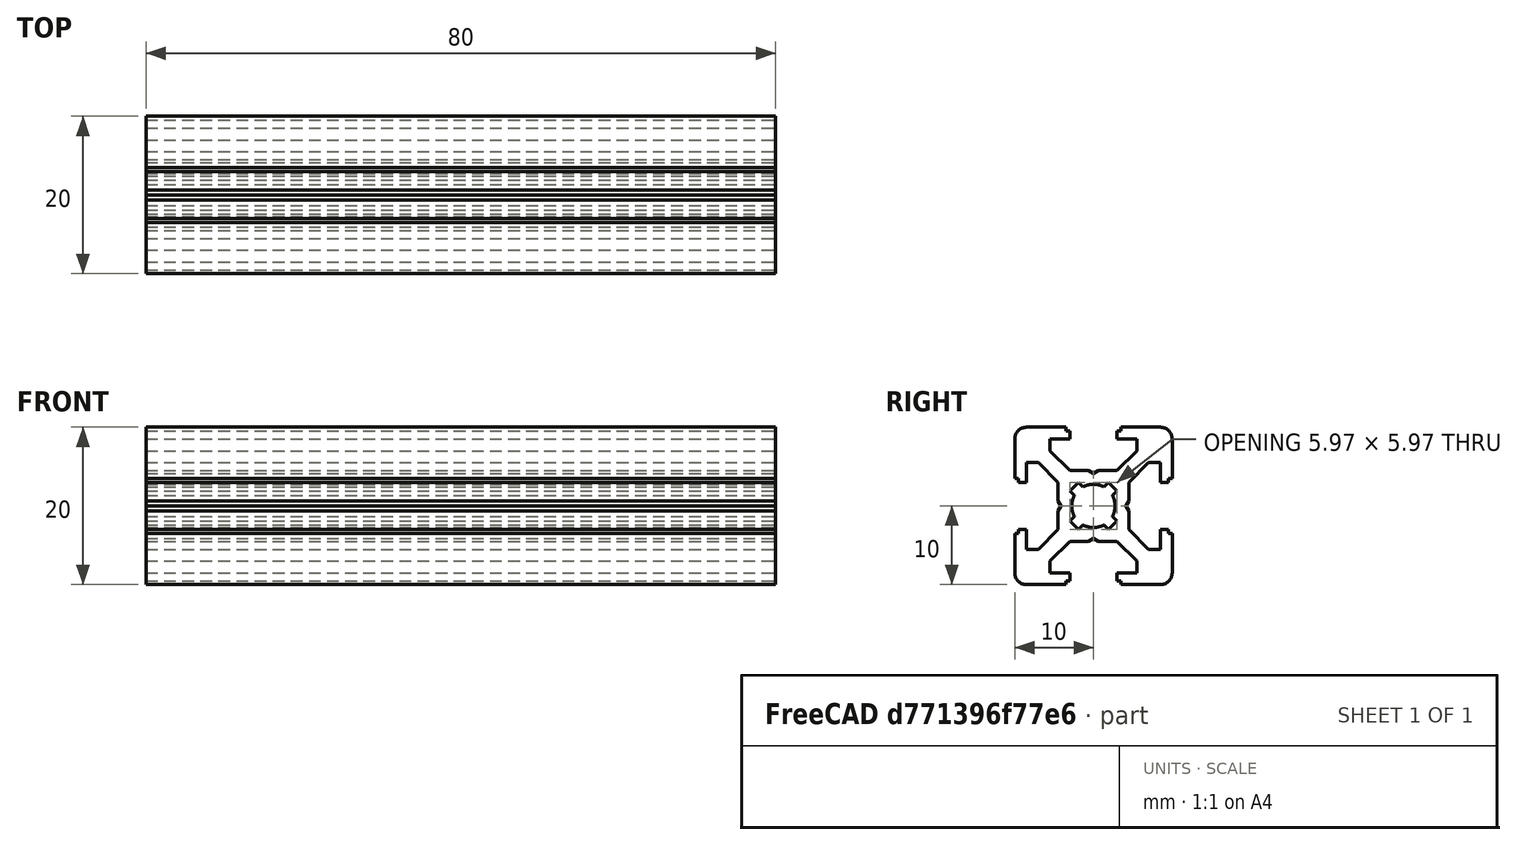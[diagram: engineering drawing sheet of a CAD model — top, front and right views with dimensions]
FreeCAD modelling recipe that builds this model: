
FCSTD DOCUMENT  (FreeCAD 0.19R)
Label: Tslot8
License: All rights reserved
LicenseURL: http://en.wikipedia.org/wiki/All_rights_reserved
objects: Sketcher::SketchObject×1, PartDesign::Pad×1, PartDesign::Body×1
note: 4 computed .brp shape members not serialized (recipe doc carries the construction recipe); baked Part::Feature solids carry a one-line shape summary decoded from their .brp

FEATURE [Sketcher::SketchObject] Sketch  label="T-Slot-Skizze"
  FullyConstrained = true
  MapMode = 5
  Placement = pos=(0,0,0) rot=(0.57735,0.57735,0.57735;2.0944rad)
  Support = -> [YZ_Plane]
  sketch-geometry (98):
    g0: LineSegment StartX=0 StartY=4.1 StartZ=0 EndX=0.65 EndY=4.5 EndZ=0
    g1: LineSegment StartX=0.65 StartY=4.5 StartZ=0 EndX=3 EndY=4.5 EndZ=0
    g2: LineSegment StartX=3 StartY=4.5 StartZ=0 EndX=5.5 EndY=7 EndZ=0
    g3: LineSegment StartX=5.5 StartY=7 StartZ=0 EndX=5.5 EndY=8.5 EndZ=0
    g4: LineSegment StartX=5.5 StartY=8.5 StartZ=0 EndX=3 EndY=8.5 EndZ=0
    g5: LineSegment StartX=3 StartY=8.5 StartZ=0 EndX=3 EndY=9.5 EndZ=0
    g6: LineSegment StartX=3 StartY=9.5 StartZ=0 EndX=3.5 EndY=9.5 EndZ=0
    g7: LineSegment StartX=3.5 StartY=9.5 StartZ=0 EndX=3.5 EndY=10 EndZ=0
    g8: LineSegment StartX=3.5 StartY=10 StartZ=0 EndX=8.5 EndY=10 EndZ=0
    g9: LineSegment StartX=10 StartY=8.5 StartZ=0 EndX=10 EndY=3.5 EndZ=0
    g10: LineSegment StartX=10 StartY=3.5 StartZ=0 EndX=9.5 EndY=3.5 EndZ=0
    g11: LineSegment StartX=9.5 StartY=3.5 StartZ=0 EndX=9.5 EndY=3 EndZ=0
    g12: LineSegment StartX=9.5 StartY=3 StartZ=0 EndX=8.5 EndY=3 EndZ=0
    g13: LineSegment StartX=8.5 StartY=3 StartZ=0 EndX=8.5 EndY=5.5 EndZ=0
    g14: LineSegment StartX=8.5 StartY=5.5 StartZ=0 EndX=7 EndY=5.5 EndZ=0
    g15: LineSegment StartX=7 StartY=5.5 StartZ=0 EndX=4.5 EndY=3 EndZ=0
    g16: LineSegment StartX=4.5 StartY=3 StartZ=0 EndX=4.5 EndY=0.65 EndZ=0
    g17: LineSegment StartX=4.5 StartY=0.65 StartZ=0 EndX=4.1 EndY=0 EndZ=0
    g18: ArcOfCircle CenterX=8.5 CenterY=8.5 CenterZ=0 NormalX=0 NormalY=0 NormalZ=1 AngleXU=0 Radius=1.5 StartAngle=0 EndAngle=1.5708
    g19: LineSegment StartX=0 StartY=-4.1 StartZ=0 EndX=0.65 EndY=-4.5 EndZ=0
    g20: LineSegment StartX=0.65 StartY=-4.5 StartZ=0 EndX=3 EndY=-4.5 EndZ=0
    g21: LineSegment StartX=3 StartY=-4.5 StartZ=0 EndX=5.5 EndY=-7 EndZ=0
    g22: LineSegment StartX=5.5 StartY=-7 StartZ=0 EndX=5.5 EndY=-8.5 EndZ=0
    g23: LineSegment StartX=5.5 StartY=-8.5 StartZ=0 EndX=3 EndY=-8.5 EndZ=0
    g24: LineSegment StartX=3 StartY=-8.5 StartZ=0 EndX=3 EndY=-9.5 EndZ=0
    g25: LineSegment StartX=3 StartY=-9.5 StartZ=0 EndX=3.5 EndY=-9.5 EndZ=0
    g26: LineSegment StartX=3.5 StartY=-9.5 StartZ=0 EndX=3.5 EndY=-10 EndZ=0
    g27: LineSegment StartX=3.5 StartY=-10 StartZ=0 EndX=8.5 EndY=-10 EndZ=0
    g28: LineSegment StartX=10 StartY=-8.5 StartZ=0 EndX=10 EndY=-3.5 EndZ=0
    g29: LineSegment StartX=10 StartY=-3.5 StartZ=0 EndX=9.5 EndY=-3.5 EndZ=0
    g30: LineSegment StartX=9.5 StartY=-3.5 StartZ=0 EndX=9.5 EndY=-3 EndZ=0
    g31: LineSegment StartX=9.5 StartY=-3 StartZ=0 EndX=8.5 EndY=-3 EndZ=0
    g32: LineSegment StartX=8.5 StartY=-3 StartZ=0 EndX=8.5 EndY=-5.5 EndZ=0
    g33: LineSegment StartX=8.5 StartY=-5.5 StartZ=0 EndX=7 EndY=-5.5 EndZ=0
    g34: LineSegment StartX=7 StartY=-5.5 StartZ=0 EndX=4.5 EndY=-3 EndZ=0
    g35: LineSegment StartX=4.5 StartY=-3 StartZ=0 EndX=4.5 EndY=-0.65 EndZ=0
    g36: ArcOfCircle CenterX=8.5 CenterY=-8.5 CenterZ=0 NormalX=0 NormalY=0 NormalZ=1 AngleXU=0 Radius=1.5 StartAngle=4.71239 EndAngle=6.28319
    g37: LineSegment StartX=4.5 StartY=-0.65 StartZ=0 EndX=4.1 EndY=0 EndZ=0
    g38: LineSegment StartX=0 StartY=-4.1 StartZ=0 EndX=-0.65 EndY=-4.5 EndZ=0
    g39: LineSegment StartX=-0.65 StartY=-4.5 StartZ=0 EndX=-3 EndY=-4.5 EndZ=0
    g40: LineSegment StartX=-3 StartY=-4.5 StartZ=0 EndX=-5.5 EndY=-7 EndZ=0
    g41: LineSegment StartX=-5.5 StartY=-7 StartZ=0 EndX=-5.5 EndY=-8.5 EndZ=0
    g42: LineSegment StartX=-5.5 StartY=-8.5 StartZ=0 EndX=-3 EndY=-8.5 EndZ=0
    g43: LineSegment StartX=-3 StartY=-8.5 StartZ=0 EndX=-3 EndY=-9.5 EndZ=0
    g44: LineSegment StartX=-3 StartY=-9.5 StartZ=0 EndX=-3.5 EndY=-9.5 EndZ=0
    g45: LineSegment StartX=-3.5 StartY=-9.5 StartZ=0 EndX=-3.5 EndY=-10 EndZ=0
    g46: LineSegment StartX=-3.5 StartY=-10 StartZ=0 EndX=-8.5 EndY=-10 EndZ=0
    g47: LineSegment StartX=-10 StartY=-8.5 StartZ=0 EndX=-10 EndY=-3.5 EndZ=0
    g48: LineSegment StartX=-10 StartY=-3.5 StartZ=0 EndX=-9.5 EndY=-3.5 EndZ=0
    g49: LineSegment StartX=-9.5 StartY=-3.5 StartZ=0 EndX=-9.5 EndY=-3 EndZ=0
    g50: LineSegment StartX=-9.5 StartY=-3 StartZ=0 EndX=-8.5 EndY=-3 EndZ=0
    g51: LineSegment StartX=-8.5 StartY=-3 StartZ=0 EndX=-8.5 EndY=-5.5 EndZ=0
    g52: LineSegment StartX=-8.5 StartY=-5.5 StartZ=0 EndX=-7 EndY=-5.5 EndZ=0
    g53: LineSegment StartX=-7 StartY=-5.5 StartZ=0 EndX=-4.5 EndY=-3 EndZ=0
    g54: LineSegment StartX=-4.5 StartY=-3 StartZ=0 EndX=-4.5 EndY=-0.65 EndZ=0
    g55: ArcOfCircle CenterX=-8.5 CenterY=-8.5 CenterZ=0 NormalX=0 NormalY=0 NormalZ=1 AngleXU=0 Radius=1.5 StartAngle=3.14159 EndAngle=4.71239
    g56: LineSegment StartX=-4.5 StartY=-0.65 StartZ=0 EndX=-4.1 EndY=0 EndZ=0
    g57: LineSegment StartX=-0.65 StartY=4.5 StartZ=0 EndX=-3 EndY=4.5 EndZ=0
    g58: LineSegment StartX=-3 StartY=4.5 StartZ=0 EndX=-5.5 EndY=7 EndZ=0
    g59: LineSegment StartX=-5.5 StartY=7 StartZ=0 EndX=-5.5 EndY=8.5 EndZ=0
    g60: LineSegment StartX=-5.5 StartY=8.5 StartZ=0 EndX=-3 EndY=8.5 EndZ=0
    g61: LineSegment StartX=-3 StartY=8.5 StartZ=0 EndX=-3 EndY=9.5 EndZ=0
    g62: LineSegment StartX=-3 StartY=9.5 StartZ=0 EndX=-3.5 EndY=9.5 EndZ=0
    g63: LineSegment StartX=-3.5 StartY=9.5 StartZ=0 EndX=-3.5 EndY=10 EndZ=0
    g64: LineSegment StartX=-3.5 StartY=10 StartZ=0 EndX=-8.5 EndY=10 EndZ=0
    g65: LineSegment StartX=-10 StartY=8.5 StartZ=0 EndX=-10 EndY=3.5 EndZ=0
    g66: LineSegment StartX=-10 StartY=3.5 StartZ=0 EndX=-9.5 EndY=3.5 EndZ=0
    g67: LineSegment StartX=-9.5 StartY=3.5 StartZ=0 EndX=-9.5 EndY=3 EndZ=0
    g68: LineSegment StartX=-9.5 StartY=3 StartZ=0 EndX=-8.5 EndY=3 EndZ=0
    g69: LineSegment StartX=-8.5 StartY=3 StartZ=0 EndX=-8.5 EndY=5.5 EndZ=0
    g70: LineSegment StartX=-8.5 StartY=5.5 StartZ=0 EndX=-7 EndY=5.5 EndZ=0
    g71: LineSegment StartX=-7 StartY=5.5 StartZ=0 EndX=-4.5 EndY=3 EndZ=0
    g72: LineSegment StartX=-4.5 StartY=3 StartZ=0 EndX=-4.5 EndY=0.65 EndZ=0
    g73: ArcOfCircle CenterX=-8.5 CenterY=8.5 CenterZ=0 NormalX=0 NormalY=0 NormalZ=1 AngleXU=0 Radius=1.5 StartAngle=1.5708 EndAngle=3.14159
    g74: LineSegment StartX=-4.5 StartY=0.65 StartZ=0 EndX=-4.1 EndY=0 EndZ=0
    g75: LineSegment StartX=0 StartY=4.1 StartZ=0 EndX=-0.65 EndY=4.5 EndZ=0
    g76: Circle CenterX=0 CenterY=0 CenterZ=0 NormalX=0 NormalY=0 NormalZ=1 AngleXU=0 Radius=3.55
    g77: Circle CenterX=0 CenterY=0 CenterZ=0 NormalX=0 NormalY=0 NormalZ=1 AngleXU=0 Radius=2.75
    g78: LineSegment StartX=1.3405 StartY=2.40116 StartZ=0 EndX=1.92324 EndY=2.9839 EndZ=0
    g79: LineSegment StartX=1.92324 StartY=2.9839 StartZ=0 EndX=2.9839 EndY=1.92324 EndZ=0
    g80: LineSegment StartX=2.9839 StartY=1.92324 StartZ=0 EndX=2.40116 EndY=1.3405 EndZ=0
    g81: ArcOfCircle CenterX=0 CenterY=0 CenterZ=0 NormalX=0 NormalY=0 NormalZ=1 AngleXU=0 Radius=2.75 StartAngle=0 EndAngle=0.509172
    g82: ArcOfCircle CenterX=0 CenterY=0 CenterZ=0 NormalX=0 NormalY=0 NormalZ=1 AngleXU=0 Radius=2.75 StartAngle=1.06162 EndAngle=1.5708
    g83: LineSegment StartX=-1.3405 StartY=2.40116 StartZ=0 EndX=-1.92324 EndY=2.9839 EndZ=0
    g84: LineSegment StartX=-1.92324 StartY=2.9839 StartZ=0 EndX=-2.9839 EndY=1.92324 EndZ=0
    g85: LineSegment StartX=-2.9839 StartY=1.92324 StartZ=0 EndX=-2.40116 EndY=1.3405 EndZ=0
    g86: ArcOfCircle CenterX=-1.3e-15 CenterY=6e-16 CenterZ=0 NormalX=0 NormalY=0 NormalZ=1 AngleXU=0 Radius=2.75 StartAngle=2.63242 EndAngle=3.14159
    g87: ArcOfCircle CenterX=-1.3e-15 CenterY=6e-16 CenterZ=0 NormalX=0 NormalY=0 NormalZ=1 AngleXU=0 Radius=2.75 StartAngle=1.5708 EndAngle=2.07997
    g88: LineSegment StartX=-1.34051 StartY=-2.40115 StartZ=0 EndX=-1.92325 EndY=-2.98389 EndZ=0
    g89: LineSegment StartX=-1.92325 StartY=-2.98389 StartZ=0 EndX=-2.9839 EndY=-1.92323 EndZ=0
    g90: LineSegment StartX=-2.9839 StartY=-1.92323 StartZ=0 EndX=-2.40116 EndY=-1.34049 EndZ=0
    g91: ArcOfCircle CenterX=-3e-16 CenterY=2e-16 CenterZ=0 NormalX=0 NormalY=0 NormalZ=1 AngleXU=0 Radius=2.75 StartAngle=3.14159 EndAngle=3.65076
    g92: ArcOfCircle CenterX=-3e-16 CenterY=2e-16 CenterZ=0 NormalX=0 NormalY=0 NormalZ=1 AngleXU=0 Radius=2.75 StartAngle=4.20321 EndAngle=4.71239
    g93: LineSegment StartX=1.34051 StartY=-2.40115 StartZ=0 EndX=1.92325 EndY=-2.98389 EndZ=0
    g94: LineSegment StartX=1.92325 StartY=-2.98389 StartZ=0 EndX=2.9839 EndY=-1.92323 EndZ=0
    g95: LineSegment StartX=2.9839 StartY=-1.92323 StartZ=0 EndX=2.40116 EndY=-1.34049 EndZ=0
    g96: ArcOfCircle CenterX=3e-16 CenterY=2e-16 CenterZ=0 NormalX=0 NormalY=0 NormalZ=1 AngleXU=0 Radius=2.75 StartAngle=4.71239 EndAngle=5.22156
    g97: ArcOfCircle CenterX=3e-16 CenterY=2e-16 CenterZ=0 NormalX=0 NormalY=0 NormalZ=1 AngleXU=0 Radius=2.75 StartAngle=5.77402 EndAngle=6.28319
  constraints (291):
    c: PointOnObject(g0,g-2)
    c: Coincident(g0,g1)
    c: Horizontal(g1)
    c: Coincident(g1,g2)
    c: Coincident(g2,g3)
    c: Vertical(g3)
    c: Coincident(g3,g4)
    c: Horizontal(g4)
    c: Coincident(g4,g5)
    c: Vertical(g5)
    c: Coincident(g5,g6)
    c: Horizontal(g6)
    c: Coincident(g6,g7)
    c: Coincident(g7,g8)
    c: Horizontal(g8)
    c: Vertical(g7)
    c: DistanceX(g-1,g5) = 3
    c: DistanceY(g4,g7) = 1.5
    c: DistanceY(g0,g7) = 5.5
    c: DistanceY(g3,g3) = 1.5
    c: DistanceY(g4,g5) = 1
    c: DistanceX(g-1,g1) = 3
    c: DistanceX(g-1,g7) = 3.5
    c: DistanceX(g0,g0) = 0.65
    c: DistanceY(g0,g0) = 0.4
    c: DistanceX(g-1,g3) = 5.5
    c: Vertical(g9)
    c: Coincident(g9,g10)
    c: Coincident(g10,g11)
    c: Coincident(g11,g12)
    c: Coincident(g12,g13)
    c: Vertical(g13)
    c: Coincident(g13,g14)
    c: Horizontal(g14)
    c: Coincident(g14,g15)
    c: Coincident(g15,g16)
    c: Vertical(g16)
    c: Coincident(g16,g17)
    c: PointOnObject(g17,g-1)
    c: Horizontal(g10)
    c: Horizontal(g12)
    c: Vertical(g11)
    c: Equal(g17,g0)
    c: Equal(g1,g16)
    c: Equal(g15,g2)
    c: Equal(g3,g14)
    c: Equal(g13,g4)
    c: Equal(g12,g5)
    c: Parallel(g15,g2)
    c: Equal(g11,g6)
    c: Equal(g10,g7)
    c: Equal(g9,g8)
    c: Tangent(g8,g18) = 1.5708
    c: Tangent(g9,g18) = 1.5708
    c: Radius(g18) = 1.5
    c: DistanceY(g-1,g8) = 10
    c: DistanceX(g-1,g9) = 10
    c: Coincident(g19,g20)
    c: Horizontal(g20)
    c: Coincident(g20,g21)
    c: Coincident(g21,g22)
    c: Vertical(g22)
    c: Coincident(g22,g23)
    c: Horizontal(g23)
    c: Coincident(g23,g24)
    c: Vertical(g24)
    c: Coincident(g24,g25)
    c: Horizontal(g25)
    c: Coincident(g25,g26)
    c: Coincident(g26,g27)
    c: Horizontal(g27)
    c: Vertical(g26)
    c: Vertical(g28)
    c: Coincident(g28,g29)
    c: Coincident(g29,g30)
    c: Coincident(g30,g31)
    c: Coincident(g31,g32)
    c: Vertical(g32)
    c: Coincident(g32,g33)
    c: Horizontal(g33)
    c: Coincident(g33,g34)
    c: Coincident(g34,g35)
    c: Vertical(g35)
    c: Coincident(g35,g37)
    c: Horizontal(g29)
    c: Horizontal(g31)
    c: Vertical(g30)
    c: Equal(g37,g19)
    c: Equal(g20,g35)
    c: Equal(g34,g21)
    c: Equal(g22,g33)
    c: Equal(g32,g23)
    c: Equal(g31,g24)
    c: Parallel(g34,g21)
    c: Equal(g30,g25)
    c: Equal(g29,g26)
    c: Equal(g28,g27)
    c: Tangent(g27,g36) = -1.5708
    c: Tangent(g28,g36) = -1.5708
    c: Radius(g36) = 1.5
    c: Equal(g9,g28)
    c: Equal(g12,g31)
    c: DistanceX(g-1,g28) = 10
    c: DistanceY(g27,g-1) = 10
    c: DistanceY(g30,g-1) = 3
    c: Equal(g33,g14)
    c: Equal(g35,g16)
    c: Equal(g17,g37)
    c: Coincident(g37,g17)
    c: Equal(g15,g34)
    c: PointOnObject(g19,g-2)
    c: DistanceY(g34,g-1) = 3
    c: DistanceX(g-1,g20) = 3
    c: Coincident(g38,g39)
    c: Horizontal(g39)
    c: Coincident(g39,g40)
    c: Coincident(g40,g41)
    c: Vertical(g41)
    c: Coincident(g41,g42)
    c: Horizontal(g42)
    c: Coincident(g42,g43)
    c: Vertical(g43)
    c: Coincident(g43,g44)
    c: Horizontal(g44)
    c: Coincident(g44,g45)
    c: Coincident(g45,g46)
    c: Horizontal(g46)
    c: Vertical(g45)
    c: Vertical(g47)
    c: Coincident(g47,g48)
    c: Coincident(g48,g49)
    c: Coincident(g49,g50)
    c: Coincident(g50,g51)
    c: Vertical(g51)
    c: Coincident(g51,g52)
    c: Horizontal(g52)
    c: Coincident(g52,g53)
    c: Coincident(g53,g54)
    c: Vertical(g54)
    c: Coincident(g54,g56)
    c: Horizontal(g48)
    c: Horizontal(g50)
    c: Vertical(g49)
    c: Equal(g39,g54)
    c: Equal(g53,g40)
    c: Equal(g41,g52)
    c: Equal(g51,g42)
    c: Equal(g50,g43)
    c: Parallel(g53,g40)
    c: Equal(g49,g44)
    c: Equal(g48,g45)
    c: Equal(g47,g46)
    c: Tangent(g46,g55) = 1.5708
    c: Tangent(g47,g55) = 1.5708
    c: Radius(g55) = 1.5
    c: Coincident(g38,g19)
    c: DistanceX(g39,g-1) = 3
    c: DistanceX(g38,g19) = 0.65
    c: DistanceY(g38,g19) = 0.4
    c: PointOnObject(g56,g-1)
    c: Equal(g56,g38)
    c: DistanceY(g53,g-1) = 3
    c: Equal(g22,g41)
    c: Equal(g42,g23)
    c: Equal(g24,g43)
    c: Equal(g25,g44)
    c: Equal(g26,g45)
    c: DistanceY(g46,g-1) = 10
    c: DistanceX(g47,g-1) = 10
    c: Coincident(g75,g57)
    c: Horizontal(g57)
    c: Coincident(g57,g58)
    c: Coincident(g58,g59)
    c: Vertical(g59)
    c: Coincident(g59,g60)
    c: Horizontal(g60)
    c: Coincident(g60,g61)
    c: Vertical(g61)
    c: Coincident(g61,g62)
    c: Horizontal(g62)
    c: Coincident(g62,g63)
    c: Coincident(g63,g64)
    c: Horizontal(g64)
    c: Vertical(g63)
    c: Vertical(g65)
    c: Coincident(g65,g66)
    c: Coincident(g66,g67)
    c: Coincident(g67,g68)
    c: Coincident(g68,g69)
    c: Vertical(g69)
    c: Coincident(g69,g70)
    c: Horizontal(g70)
    c: Coincident(g70,g71)
    c: Coincident(g71,g72)
    c: Vertical(g72)
    c: Coincident(g72,g74)
    c: Horizontal(g66)
    c: Horizontal(g68)
    c: Vertical(g67)
    c: Equal(g57,g72)
    c: Equal(g71,g58)
    c: Equal(g59,g70)
    c: Equal(g69,g60)
    c: Equal(g68,g61)
    c: Parallel(g71,g58)
    c: Equal(g67,g62)
    c: Equal(g66,g63)
    c: Equal(g65,g64)
    c: Tangent(g64,g73) = -1.5708
    c: Tangent(g65,g73) = -1.5708
    c: Radius(g73) = 1.5
    c: Equal(g74,g75)
    c: Coincident(g56,g74)
    c: Coincident(g0,g75)
    c: Equal(g0,g75)
    c: Equal(g1,g57)
    c: Equal(g2,g58)
    c: Equal(g3,g59)
    c: Equal(g4,g60)
    c: Equal(g5,g61)
    c: Equal(g6,g62)
    c: Equal(g7,g63)
    c: Equal(g8,g64)
    c: DistanceX(g65,g-1) = 10
    c: Coincident(g76,g-1)
    c: Coincident(g77,g-1)
    c: Radius(g76) = 3.55
    c: Radius(g77) = 2.75
    c: PointOnObject(g78,g77)
    c: PointOnObject(g78,g76)
    c: Coincident(g78,g79)
    c: PointOnObject(g79,g76)
    c: Coincident(g79,g80)
    c: PointOnObject(g80,g77)
    c: Coincident(g81,g-1)
    c: Coincident(g81,g80)
    c: Coincident(g82,g81)
    c: Coincident(g82,g78)
    c: Parallel(g78,g80)
    c: Parallel(g78,g2)
    c: Distance(g79) = 1.5
    c: Distance(g78,g80) = 1.5
    c: PointOnObject(g82,g-2)
    c: PointOnObject(g81,g-1)
    c: Coincident(g83,g84)
    c: Coincident(g84,g85)
    c: Coincident(g86,g85)
    c: Coincident(g87,g86)
    c: Coincident(g87,g83)
    c: Parallel(g83,g85)
    c: Distance(g84) = 1.5
    c: Distance(g83,g85) = 1.5
    c: Coincident(g82,g87)
    c: PointOnObject(g86,g-1)
    c: PointOnObject(g83,g76)
    c: PointOnObject(g83,g77)
    c: PointOnObject(g85,g77)
    c: PointOnObject(g84,g76)
    c: PointOnObject(g86,g77)
    c: Parallel(g85,g71)
    c: Coincident(g88,g89)
    c: Coincident(g89,g90)
    c: Coincident(g91,g90)
    c: Coincident(g92,g91)
    c: Coincident(g92,g88)
    c: Parallel(g88,g90)
    c: Distance(g89) = 1.5
    c: Distance(g88,g90) = 1.5
    c: PointOnObject(g88,g77)
    c: PointOnObject(g90,g77)
    c: Coincident(g86,g91)
    c: PointOnObject(g89,g76)
    c: PointOnObject(g88,g76)
    c: PointOnObject(g92,g-2)
    c: PointOnObject(g92,g77)
    c: Parallel(g88,g40)
    c: Coincident(g93,g94)
    c: Coincident(g94,g95)
    c: Coincident(g97,g95)
    c: Coincident(g96,g97)
    c: Coincident(g96,g93)
    c: Parallel(g93,g95)
    c: Distance(g94) = 1.5
    c: Distance(g93,g95) = 1.5
    c: Coincident(g81,g97)
    c: Coincident(g92,g96)
    c: PointOnObject(g93,g77)
    c: PointOnObject(g95,g77)
    c: PointOnObject(g94,g76)
    c: PointOnObject(g93,g76)
    c: Parallel(g93,g21)
FEATURE [PartDesign::Pad] Pad  label="T-Slot-Element"
  Direction = (1,1,1)
  Length = 80
  Length2 = 100
  Placement = pos=(0,0,0) rot=(0.57735,0.57735,0.57735;2.0944rad)
  Profile = -> Sketch
  Type = 0
FEATURE [PartDesign::Body] Body  label="T-Slot-Profil 20x20"
  Group = -> [Sketch,Pad]
  Origin = -> Origin
  Tip = -> Pad
